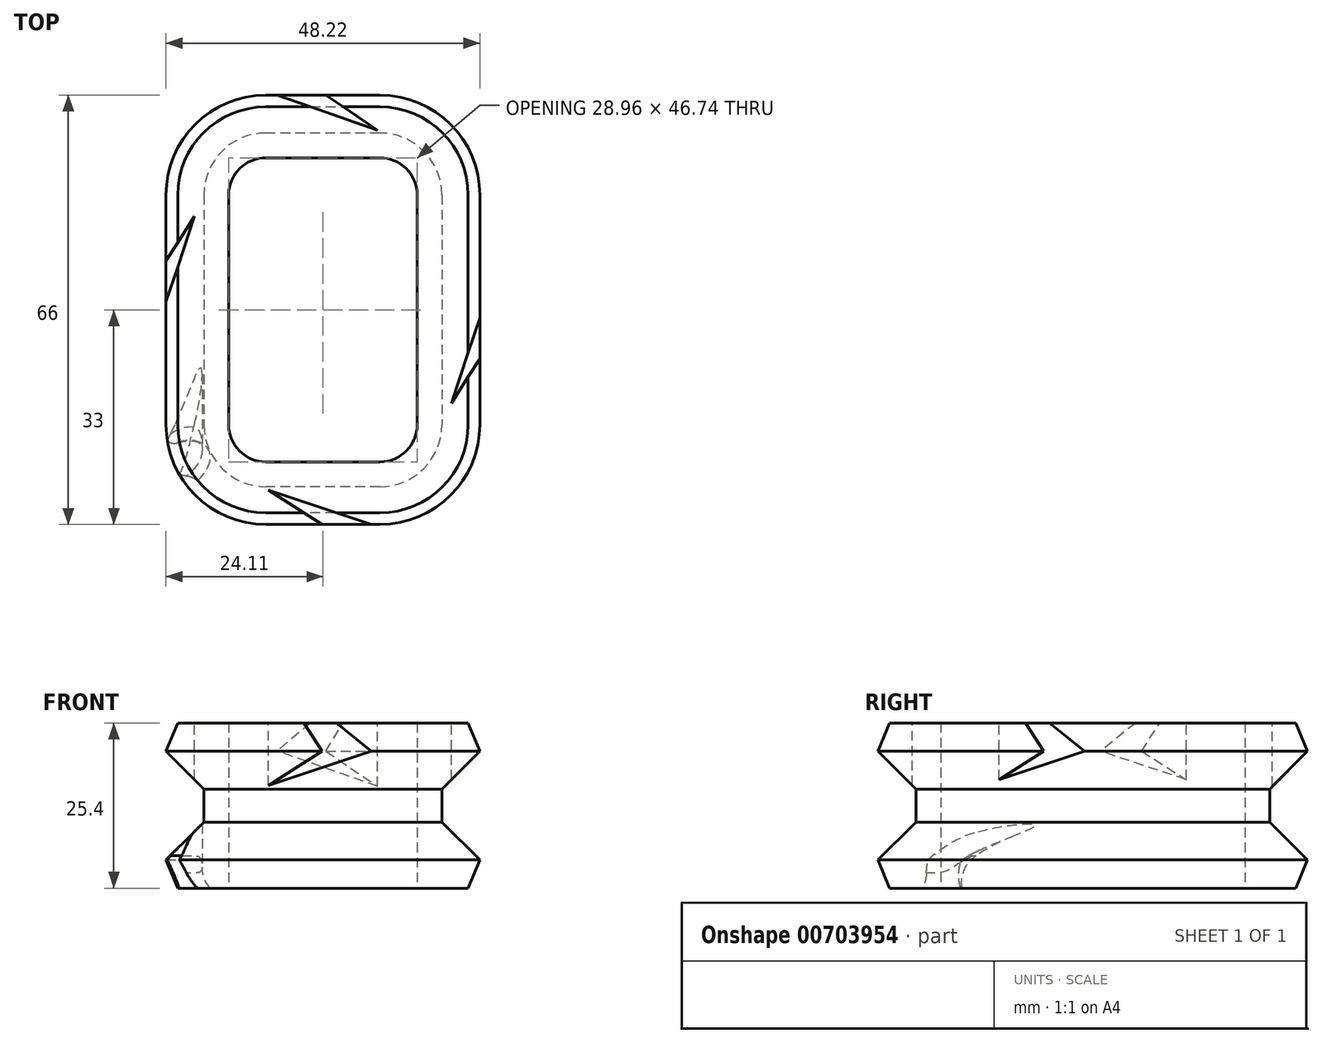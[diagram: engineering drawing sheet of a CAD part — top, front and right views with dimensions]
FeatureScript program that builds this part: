
annotation { "Feature Type Name" : "Feature", "Feature Type Description" : "" }
export const myFeature = defineFeature(function(context is Context, id is Id, definition is map)
    precondition{}
    {
        {
            var Q0;
            Q0=qCreatedBy(makeId("Top.planeOp"),FACE);
            var sketch = newSketch(context, id + "F0", { "sketchPlane" : qUnion([Q0])});
            skLineSegment(sketch, "E0.bottom", {"start": v(8.76, 23.37) * mm, "end": v(-8.76, 23.37) * mm});
            skLineSegment(sketch, "E0.top", {"start": v(8.76, -23.37) * mm, "end": v(-8.76, -23.37) * mm});
            skLineSegment(sketch, "E0.left", {"start": v(14.48, 17.65) * mm, "end": v(14.48, -17.65) * mm});
            skLineSegment(sketch, "E0.right", {"start": v(-14.48, 17.65) * mm, "end": v(-14.48, -17.65) * mm});
            skPoint(sketch, "E0.middle", {"position": v(0, 0) * mm});
            skPoint(sketch, "E1.visualSharp", {"position": v(-14.48, 23.37) * mm});
            skArc(sketch, "E1.filletArc", {"start": v(-8.76, 23.37) * mm, "mid": v(-12.8, 21.7) * mm, "end": v(-14.48, 17.65) * mm});
            skPoint(sketch, "E2.visualSharp", {"position": v(14.48, 23.37) * mm});
            skArc(sketch, "E2.filletArc", {"start": v(14.48, 17.65) * mm, "mid": v(12.8, 21.7) * mm, "end": v(8.76, 23.37) * mm});
            skPoint(sketch, "E3.visualSharp", {"position": v(14.48, -23.37) * mm});
            skArc(sketch, "E3.filletArc", {"start": v(8.76, -23.37) * mm, "mid": v(12.8, -21.7) * mm, "end": v(14.48, -17.65) * mm});
            skPoint(sketch, "E4.visualSharp", {"position": v(-14.48, -23.37) * mm});
            skArc(sketch, "E4.filletArc", {"start": v(-14.48, -17.65) * mm, "mid": v(-12.8, -21.7) * mm, "end": v(-8.76, -23.37) * mm});
            skLineSegment(sketch, "E5.0", {"start": v(-18.29, 17.65) * mm, "end": v(-18.29, -17.65) * mm});
            skArc(sketch, "E5.1", {"start": v(-8.76, 27.18) * mm, "mid": v(-15.5, 24.39) * mm, "end": v(-18.29, 17.65) * mm});
            skArc(sketch, "E5.2", {"start": v(-18.29, -17.65) * mm, "mid": v(-15.5, -24.39) * mm, "end": v(-8.76, -27.18) * mm});
            skLineSegment(sketch, "E5.3", {"start": v(8.76, 27.18) * mm, "end": v(-8.76, 27.18) * mm});
            skLineSegment(sketch, "E5.4", {"start": v(8.76, -27.18) * mm, "end": v(-8.76, -27.18) * mm});
            skArc(sketch, "E5.5", {"start": v(8.76, -27.18) * mm, "mid": v(15.5, -24.39) * mm, "end": v(18.29, -17.65) * mm});
            skLineSegment(sketch, "E5.6", {"start": v(18.29, 17.65) * mm, "end": v(18.29, -17.65) * mm});
            skArc(sketch, "E5.7", {"start": v(18.29, 17.65) * mm, "mid": v(15.5, 24.39) * mm, "end": v(8.76, 27.18) * mm});
            skArc(sketch, "E6.0", {"start": v(28.45, 17.65) * mm, "mid": v(22.68, 31.57) * mm, "end": v(8.76, 37.34) * mm});
            skLineSegment(sketch, "E6.1", {"start": v(28.45, 17.65) * mm, "end": v(28.45, -17.65) * mm});
            skLineSegment(sketch, "E6.2", {"start": v(8.76, 37.34) * mm, "end": v(-8.76, 37.34) * mm});
            skArc(sketch, "E6.3", {"start": v(8.76, -37.34) * mm, "mid": v(22.68, -31.57) * mm, "end": v(28.45, -17.65) * mm});
            skArc(sketch, "E6.4", {"start": v(-8.76, 37.34) * mm, "mid": v(-22.68, 31.57) * mm, "end": v(-28.45, 17.65) * mm});
            skLineSegment(sketch, "E6.5", {"start": v(-28.45, 17.65) * mm, "end": v(-28.45, -17.65) * mm});
            skArc(sketch, "E6.6", {"start": v(-28.45, -17.65) * mm, "mid": v(-22.68, -31.57) * mm, "end": v(-8.76, -37.34) * mm});
            skLineSegment(sketch, "E6.7", {"start": v(8.76, -37.34) * mm, "end": v(-8.76, -37.34) * mm});
            skSolve(sketch);
        }
        {
            var Q0;
            Q0=makeQuery(id+"F0.imprint","IMPRINT",FACE,{"disambiguationData":[TD([[makeQuery(id+"F0.imprint","IMPRINT",EDGE,{"derivedFrom":sQuery(id+"F0.wireOp",EDGE,"E0.bottom")}),-1.0]])]});
            extrude(context, id + "F1", {"entities" : qUnion([Q0]), "depth" : 25.4 * mm, "offsetDistance" : 25.4 * mm});
        }
        {
            var Q0;
            Q0=qCreatedBy(makeId("Top.planeOp"),FACE);
            cPlane(context, id + "F2", {"entities" : qUnion([Q0]), "cplaneType" : CPlaneType.OFFSET, "offset" : 25.4 * mm, "width" : 152.4 * mm, "height" : 152.4 * mm});
        }
        {
            var Q0;
            Q0=makeQuery(id+"F0.imprint","IMPRINT",FACE,{"disambiguationData":[TD([[makeQuery(id+"F0.imprint","IMPRINT",EDGE,{"derivedFrom":sQuery(id+"F0.wireOp",EDGE,"E5.0")}),-1.0]])]});
            extrude(context, id + "F3", {"entities" : qUnion([Q0]), "operationType" : NewBodyOperationType.ADD, "depth" : 10.16 * mm, "offsetDistance" : 25.4 * mm});
        }
        {
            var Q0;
            Q0=makeQuery(id+"F3.opExtrude","CAP_EDGE",EDGE,{"disambiguationData":[OSD([sQuery(id+"F0.wireOp",EDGE,"E6.7")])],"isStart":false});
            chamfer(context, id + "F4", {"entities" : qUnion([Q0]), "width" : 10.16 * mm, "tangentPropagation" : true});
        }
        {
            var Q0;
            {var subQ0=sQuery(id+"F0.wireOp",EDGE,"E6.3");var subQ1=sQuery(id+"F0.wireOp",EDGE,"E5.7");var subQ2=sQuery(id+"F0.wireOp",EDGE,"E5.6");var subQ3=sQuery(id+"F0.wireOp",EDGE,"E5.5");var subQ4=sQuery(id+"F0.wireOp",EDGE,"E5.4");var subQ5=sQuery(id+"F0.wireOp",EDGE,"E5.3");var subQ6=sQuery(id+"F0.wireOp",EDGE,"E5.2");var subQ7=sQuery(id+"F0.wireOp",EDGE,"E5.1");var subQ8=sQuery(id+"F0.wireOp",EDGE,"E5.0");Q0=makeQuery(id+"F4.opChamfer","BLEND_EDGE",EDGE,{"blendedFrom":[makeQuery(id+"F3.opExtrude","CAP_EDGE",EDGE,{"disambiguationData":[OSD([subQ0])],"isStart":false}),makeQuery(id+"F3.boolean.opBoolean","MERGE",FACE,{"derivedFrom":[makeQuery(id+"F1.opExtrude","CAP_FACE",FACE,{"disambiguationData":[OSD([sQuery(id+"F0.wireOp",EDGE,"E0.bottom"),sQuery(id+"F0.wireOp",EDGE,"E0.top"),sQuery(id+"F0.wireOp",EDGE,"E0.left"),sQuery(id+"F0.wireOp",EDGE,"E0.right"),sQuery(id+"F0.wireOp",EDGE,"E1.filletArc"),sQuery(id+"F0.wireOp",EDGE,"E2.filletArc"),sQuery(id+"F0.wireOp",EDGE,"E3.filletArc"),sQuery(id+"F0.wireOp",EDGE,"E4.filletArc"),subQ8,subQ7,subQ6,subQ5,subQ4,subQ3,subQ2,subQ1])],"isStart":true}),makeQuery(id+"F3.opExtrude","CAP_FACE",FACE,{"disambiguationData":[OSD([subQ8,subQ7,subQ6,subQ5,subQ4,subQ3,subQ2,subQ1,sQuery(id+"F0.wireOp",EDGE,"E6.0"),sQuery(id+"F0.wireOp",EDGE,"E6.1"),sQuery(id+"F0.wireOp",EDGE,"E6.2"),subQ0,sQuery(id+"F0.wireOp",EDGE,"E6.4"),sQuery(id+"F0.wireOp",EDGE,"E6.5"),sQuery(id+"F0.wireOp",EDGE,"E6.6"),sQuery(id+"F0.wireOp",EDGE,"E6.7")])],"isStart":true})]})],"blendedInto":[makeQuery(id+"F3.boolean.opBoolean","MERGE",FACE,{"derivedFrom":[makeQuery(id+"F1.opExtrude","CAP_FACE",FACE,{"disambiguationData":[OSD([sQuery(id+"F0.wireOp",EDGE,"E0.bottom"),sQuery(id+"F0.wireOp",EDGE,"E0.top"),sQuery(id+"F0.wireOp",EDGE,"E0.left"),sQuery(id+"F0.wireOp",EDGE,"E0.right"),sQuery(id+"F0.wireOp",EDGE,"E1.filletArc"),sQuery(id+"F0.wireOp",EDGE,"E2.filletArc"),sQuery(id+"F0.wireOp",EDGE,"E3.filletArc"),sQuery(id+"F0.wireOp",EDGE,"E4.filletArc"),subQ8,subQ7,subQ6,subQ5,subQ4,subQ3,subQ2,subQ1])],"isStart":true}),makeQuery(id+"F3.opExtrude","CAP_FACE",FACE,{"disambiguationData":[OSD([subQ8,subQ7,subQ6,subQ5,subQ4,subQ3,subQ2,subQ1,sQuery(id+"F0.wireOp",EDGE,"E6.0"),sQuery(id+"F0.wireOp",EDGE,"E6.1"),sQuery(id+"F0.wireOp",EDGE,"E6.2"),subQ0,sQuery(id+"F0.wireOp",EDGE,"E6.4"),sQuery(id+"F0.wireOp",EDGE,"E6.5"),sQuery(id+"F0.wireOp",EDGE,"E6.6"),sQuery(id+"F0.wireOp",EDGE,"E6.7")])],"isStart":true})]})]});}
            chamfer(context, id + "F5", {"entities" : qUnion([Q0]), "width" : 2.54 * mm, "tangentPropagation" : true});
        }
        {
            var Q0;
            Q0=qCreatedBy(id+"F2.planeOp",FACE);
            var sketch = newSketch(context, id + "F6", { "sketchPlane" : qUnion([Q0])});
            skArc(sketch, "E7.0", {"start": v(28.45, 17.65) * mm, "mid": v(22.68, 31.57) * mm, "end": v(8.76, 37.34) * mm});
            skLineSegment(sketch, "E7.1", {"start": v(28.45, 17.65) * mm, "end": v(28.45, -17.65) * mm});
            skLineSegment(sketch, "E7.2", {"start": v(8.76, 37.34) * mm, "end": v(-8.76, 37.34) * mm});
            skArc(sketch, "E7.3", {"start": v(8.76, -37.34) * mm, "mid": v(22.68, -31.57) * mm, "end": v(28.45, -17.65) * mm});
            skArc(sketch, "E7.4", {"start": v(-8.76, 37.34) * mm, "mid": v(-22.68, 31.57) * mm, "end": v(-28.45, 17.65) * mm});
            skLineSegment(sketch, "E7.5", {"start": v(-28.45, 17.65) * mm, "end": v(-28.45, -17.65) * mm});
            skArc(sketch, "E7.6", {"start": v(-28.45, -17.65) * mm, "mid": v(-22.68, -31.57) * mm, "end": v(-8.76, -37.34) * mm});
            skLineSegment(sketch, "E7.7", {"start": v(8.76, -37.34) * mm, "end": v(-8.76, -37.34) * mm});
            skLineSegment(sketch, "E8.0", {"start": v(8.76, 27.18) * mm, "end": v(-8.76, 27.18) * mm});
            skArc(sketch, "E8.1", {"start": v(18.29, 17.65) * mm, "mid": v(15.5, 24.39) * mm, "end": v(8.76, 27.18) * mm});
            skArc(sketch, "E8.2", {"start": v(-8.76, 27.18) * mm, "mid": v(-15.5, 24.39) * mm, "end": v(-18.29, 17.65) * mm});
            skLineSegment(sketch, "E8.3", {"start": v(18.29, 17.65) * mm, "end": v(18.29, -17.65) * mm});
            skLineSegment(sketch, "E8.4", {"start": v(-18.29, 17.65) * mm, "end": v(-18.29, -17.65) * mm});
            skArc(sketch, "E8.5", {"start": v(-18.29, -17.65) * mm, "mid": v(-15.5, -24.39) * mm, "end": v(-8.76, -27.18) * mm});
            skLineSegment(sketch, "E8.6", {"start": v(8.76, -27.18) * mm, "end": v(-8.76, -27.18) * mm});
            skArc(sketch, "E8.7", {"start": v(8.76, -27.18) * mm, "mid": v(15.5, -24.39) * mm, "end": v(18.29, -17.65) * mm});
            skSolve(sketch);
        }
        {
            var Q0;
            Q0=makeQuery(id+"F6.imprint","IMPRINT",FACE,{"disambiguationData":[TD([[makeQuery(id+"F6.imprint","IMPRINT",EDGE,{"derivedFrom":sQuery(id+"F6.wireOp",EDGE,"E7.0")}),1.0]])]});
            extrude(context, id + "F7", {"entities" : qUnion([Q0]), "operationType" : NewBodyOperationType.ADD, "oppositeDirection" : true, "depth" : 10.16 * mm, "offsetDistance" : 25.4 * mm});
        }
        {
            var Q0;
            Q0=makeQuery(id+"F7.opExtrude","CAP_EDGE",EDGE,{"disambiguationData":[OSD([sQuery(id+"F6.wireOp",EDGE,"E7.7")])],"isStart":false});
            chamfer(context, id + "F8", {"entities" : qUnion([Q0]), "width" : 10.16 * mm, "tangentPropagation" : true});
        }
        {
            var Q0;
            {var subQ0=sQuery(id+"F6.wireOp",EDGE,"E7.7");Q0=makeQuery(id+"F8.opChamfer","BLEND_EDGE",EDGE,{"blendedFrom":[makeQuery(id+"F7.opExtrude","CAP_EDGE",EDGE,{"disambiguationData":[OSD([subQ0])],"isStart":false}),makeQuery(id+"F7.boolean.opBoolean","MERGE",FACE,{"derivedFrom":[makeQuery(id+"F1.opExtrude","CAP_FACE",FACE,{"disambiguationData":[OSD([sQuery(id+"F0.wireOp",EDGE,"E0.bottom"),sQuery(id+"F0.wireOp",EDGE,"E0.top"),sQuery(id+"F0.wireOp",EDGE,"E0.left"),sQuery(id+"F0.wireOp",EDGE,"E0.right"),sQuery(id+"F0.wireOp",EDGE,"E1.filletArc"),sQuery(id+"F0.wireOp",EDGE,"E2.filletArc"),sQuery(id+"F0.wireOp",EDGE,"E3.filletArc"),sQuery(id+"F0.wireOp",EDGE,"E4.filletArc"),sQuery(id+"F0.wireOp",EDGE,"E5.0"),sQuery(id+"F0.wireOp",EDGE,"E5.1"),sQuery(id+"F0.wireOp",EDGE,"E5.2"),sQuery(id+"F0.wireOp",EDGE,"E5.3"),sQuery(id+"F0.wireOp",EDGE,"E5.4"),sQuery(id+"F0.wireOp",EDGE,"E5.5"),sQuery(id+"F0.wireOp",EDGE,"E5.6"),sQuery(id+"F0.wireOp",EDGE,"E5.7")])],"isStart":false}),makeQuery(id+"F7.opExtrude","CAP_FACE",FACE,{"disambiguationData":[OSD([sQuery(id+"F6.wireOp",EDGE,"E7.0"),sQuery(id+"F6.wireOp",EDGE,"E7.1"),sQuery(id+"F6.wireOp",EDGE,"E7.2"),sQuery(id+"F6.wireOp",EDGE,"E7.3"),sQuery(id+"F6.wireOp",EDGE,"E7.4"),sQuery(id+"F6.wireOp",EDGE,"E7.5"),sQuery(id+"F6.wireOp",EDGE,"E7.6"),subQ0,sQuery(id+"F6.wireOp",EDGE,"E8.0"),sQuery(id+"F6.wireOp",EDGE,"E8.1"),sQuery(id+"F6.wireOp",EDGE,"E8.2"),sQuery(id+"F6.wireOp",EDGE,"E8.3"),sQuery(id+"F6.wireOp",EDGE,"E8.4"),sQuery(id+"F6.wireOp",EDGE,"E8.5"),sQuery(id+"F6.wireOp",EDGE,"E8.6"),sQuery(id+"F6.wireOp",EDGE,"E8.7")])],"isStart":true})]})],"blendedInto":[makeQuery(id+"F7.boolean.opBoolean","MERGE",FACE,{"derivedFrom":[makeQuery(id+"F1.opExtrude","CAP_FACE",FACE,{"disambiguationData":[OSD([sQuery(id+"F0.wireOp",EDGE,"E0.bottom"),sQuery(id+"F0.wireOp",EDGE,"E0.top"),sQuery(id+"F0.wireOp",EDGE,"E0.left"),sQuery(id+"F0.wireOp",EDGE,"E0.right"),sQuery(id+"F0.wireOp",EDGE,"E1.filletArc"),sQuery(id+"F0.wireOp",EDGE,"E2.filletArc"),sQuery(id+"F0.wireOp",EDGE,"E3.filletArc"),sQuery(id+"F0.wireOp",EDGE,"E4.filletArc"),sQuery(id+"F0.wireOp",EDGE,"E5.0"),sQuery(id+"F0.wireOp",EDGE,"E5.1"),sQuery(id+"F0.wireOp",EDGE,"E5.2"),sQuery(id+"F0.wireOp",EDGE,"E5.3"),sQuery(id+"F0.wireOp",EDGE,"E5.4"),sQuery(id+"F0.wireOp",EDGE,"E5.5"),sQuery(id+"F0.wireOp",EDGE,"E5.6"),sQuery(id+"F0.wireOp",EDGE,"E5.7")])],"isStart":false}),makeQuery(id+"F7.opExtrude","CAP_FACE",FACE,{"disambiguationData":[OSD([sQuery(id+"F6.wireOp",EDGE,"E7.0"),sQuery(id+"F6.wireOp",EDGE,"E7.1"),sQuery(id+"F6.wireOp",EDGE,"E7.2"),sQuery(id+"F6.wireOp",EDGE,"E7.3"),sQuery(id+"F6.wireOp",EDGE,"E7.4"),sQuery(id+"F6.wireOp",EDGE,"E7.5"),sQuery(id+"F6.wireOp",EDGE,"E7.6"),subQ0,sQuery(id+"F6.wireOp",EDGE,"E8.0"),sQuery(id+"F6.wireOp",EDGE,"E8.1"),sQuery(id+"F6.wireOp",EDGE,"E8.2"),sQuery(id+"F6.wireOp",EDGE,"E8.3"),sQuery(id+"F6.wireOp",EDGE,"E8.4"),sQuery(id+"F6.wireOp",EDGE,"E8.5"),sQuery(id+"F6.wireOp",EDGE,"E8.6"),sQuery(id+"F6.wireOp",EDGE,"E8.7")])],"isStart":true})]})]});}
            chamfer(context, id + "F9", {"entities" : qUnion([Q0]), "width" : 2.54 * mm, "tangentPropagation" : true});
        }
        {
            var Q0;
            Q0=qCreatedBy(makeId("Right.planeOp"),FACE);
            cPlane(context, id + "F10", {"entities" : qUnion([Q0]), "cplaneType" : CPlaneType.OFFSET, "offset" : 20.32 * mm, "oppositeDirection" : true, "width" : 152.4 * mm, "height" : 152.4 * mm});
        }
        {
            var Q0;
            Q0=qCreatedBy(id+"F10.planeOp",FACE);
            var sketch = newSketch(context, id + "F11", { "sketchPlane" : qUnion([Q0])});
            skFitSpline(sketch, "E9", {"points": [v(-24.66, -12.7) * mm, v(-21.88, 3.4) * mm, v(0, 12.85) * mm, v(9.24, 13.4) * mm], "startDerivative": vector(2.56, 51.63) * mm, "endDerivative": vector(30.58, -0.85) * mm});
            skSolve(sketch);
        }
        {
            var Q0;
            Q0=qCreatedBy(makeId("Top.planeOp"),FACE);
            cPlane(context, id + "F12", {"entities" : qUnion([Q0]), "cplaneType" : CPlaneType.OFFSET, "offset" : 7.62 * mm, "oppositeDirection" : true, "width" : 152.4 * mm, "height" : 152.4 * mm});
        }
        {
            var Q0;
            Q0=qCreatedBy(id+"F12.planeOp",FACE);
            var sketch = newSketch(context, id + "F13", { "sketchPlane" : qUnion([Q0])});
            skFitSpline(sketch, "E10", {"points": [v(-29.95, -29.23) * mm, v(-23.21, -23.7) * mm, v(-18.64, -23.8) * mm, v(-22.25, -28.06) * mm, v(-30.23, -30.68) * mm, v(-29.95, -29.23) * mm]});
            skSolve(sketch);
        }
        {
            var Q0;
            Q0=makeQuery(id+"F13.imprint","IMPRINT",FACE,{"disambiguationData":[TD([[makeQuery(id+"F13.imprint","IMPRINT",EDGE,{"derivedFrom":sQuery(id+"F13.wireOp",EDGE,"E10")}),-1.0]])]});
            var Q1;
            Q1=sQuery(id+"F11.wireOp",EDGE,"E9");
            sweep(context, id + "F14", {"operationType" : NewBodyOperationType.REMOVE, "profiles" : qUnion([Q0]), "path" : qUnion([Q1])});
        }
        {
            var Q0;
            {var subQ0=sQuery(id+"F0.wireOp",EDGE,"E5.7");var subQ1=sQuery(id+"F0.wireOp",EDGE,"E5.6");var subQ2=sQuery(id+"F0.wireOp",EDGE,"E5.5");var subQ3=sQuery(id+"F0.wireOp",EDGE,"E5.4");var subQ4=sQuery(id+"F0.wireOp",EDGE,"E5.3");var subQ5=sQuery(id+"F0.wireOp",EDGE,"E5.2");var subQ6=sQuery(id+"F0.wireOp",EDGE,"E5.1");var subQ7=sQuery(id+"F0.wireOp",EDGE,"E5.0");Q0=makeQuery(id+"F14.boolean.opBoolean","INTERSECT",EDGE,{"derivedFrom":[makeQuery(id+"F3.boolean.opBoolean","MERGE",FACE,{"derivedFrom":[makeQuery(id+"F1.opExtrude","CAP_FACE",FACE,{"disambiguationData":[OSD([sQuery(id+"F0.wireOp",EDGE,"E0.bottom"),sQuery(id+"F0.wireOp",EDGE,"E0.top"),sQuery(id+"F0.wireOp",EDGE,"E0.left"),sQuery(id+"F0.wireOp",EDGE,"E0.right"),sQuery(id+"F0.wireOp",EDGE,"E1.filletArc"),sQuery(id+"F0.wireOp",EDGE,"E2.filletArc"),sQuery(id+"F0.wireOp",EDGE,"E3.filletArc"),sQuery(id+"F0.wireOp",EDGE,"E4.filletArc"),subQ7,subQ6,subQ5,subQ4,subQ3,subQ2,subQ1,subQ0])],"isStart":true}),makeQuery(id+"F3.opExtrude","CAP_FACE",FACE,{"disambiguationData":[OSD([subQ7,subQ6,subQ5,subQ4,subQ3,subQ2,subQ1,subQ0,sQuery(id+"F0.wireOp",EDGE,"E6.0"),sQuery(id+"F0.wireOp",EDGE,"E6.1"),sQuery(id+"F0.wireOp",EDGE,"E6.2"),sQuery(id+"F0.wireOp",EDGE,"E6.3"),sQuery(id+"F0.wireOp",EDGE,"E6.4"),sQuery(id+"F0.wireOp",EDGE,"E6.5"),sQuery(id+"F0.wireOp",EDGE,"E6.6"),sQuery(id+"F0.wireOp",EDGE,"E6.7")])],"isStart":true})]}),makeQuery(id+"F14.opSweep","SWEPT_FACE",FACE,{"disambiguationData":[OSD([sQuery(id+"F11.wireOp",EDGE,"E9"),sQuery(id+"F13.wireOp",EDGE,"E10")])]})]});}
            chamfer(context, id + "F15", {"entities" : qUnion([Q0]), "width" : 1.27 * mm, "tangentPropagation" : true});
        }
        {
            var Q0;
            {var subQ0=makeQuery(id+"F14.opSweep","SWEPT_FACE",FACE,{"disambiguationData":[OSD([sQuery(id+"F11.wireOp",EDGE,"E9"),sQuery(id+"F13.wireOp",EDGE,"E10")])]});var subQ1=sQuery(id+"F0.wireOp",EDGE,"E5.7");var subQ2=sQuery(id+"F0.wireOp",EDGE,"E5.6");var subQ3=sQuery(id+"F0.wireOp",EDGE,"E5.5");var subQ4=sQuery(id+"F0.wireOp",EDGE,"E5.4");var subQ5=sQuery(id+"F0.wireOp",EDGE,"E5.3");var subQ6=sQuery(id+"F0.wireOp",EDGE,"E5.2");var subQ7=sQuery(id+"F0.wireOp",EDGE,"E5.1");var subQ8=sQuery(id+"F0.wireOp",EDGE,"E5.0");Q0=makeQuery(id+"F15.opChamfer","BLEND_EDGE",EDGE,{"blendedFrom":[makeQuery(id+"F14.boolean.opBoolean","INTERSECT",EDGE,{"derivedFrom":[makeQuery(id+"F3.boolean.opBoolean","MERGE",FACE,{"derivedFrom":[makeQuery(id+"F1.opExtrude","CAP_FACE",FACE,{"disambiguationData":[OSD([sQuery(id+"F0.wireOp",EDGE,"E0.bottom"),sQuery(id+"F0.wireOp",EDGE,"E0.top"),sQuery(id+"F0.wireOp",EDGE,"E0.left"),sQuery(id+"F0.wireOp",EDGE,"E0.right"),sQuery(id+"F0.wireOp",EDGE,"E1.filletArc"),sQuery(id+"F0.wireOp",EDGE,"E2.filletArc"),sQuery(id+"F0.wireOp",EDGE,"E3.filletArc"),sQuery(id+"F0.wireOp",EDGE,"E4.filletArc"),subQ8,subQ7,subQ6,subQ5,subQ4,subQ3,subQ2,subQ1])],"isStart":true}),makeQuery(id+"F3.opExtrude","CAP_FACE",FACE,{"disambiguationData":[OSD([subQ8,subQ7,subQ6,subQ5,subQ4,subQ3,subQ2,subQ1,sQuery(id+"F0.wireOp",EDGE,"E6.0"),sQuery(id+"F0.wireOp",EDGE,"E6.1"),sQuery(id+"F0.wireOp",EDGE,"E6.2"),sQuery(id+"F0.wireOp",EDGE,"E6.3"),sQuery(id+"F0.wireOp",EDGE,"E6.4"),sQuery(id+"F0.wireOp",EDGE,"E6.5"),sQuery(id+"F0.wireOp",EDGE,"E6.6"),sQuery(id+"F0.wireOp",EDGE,"E6.7")])],"isStart":true})]}),subQ0]}),makeQuery(id+"F14.boolean.opBoolean","COPY",FACE,{"derivedFrom":subQ0})],"blendedInto":[makeQuery(id+"F14.boolean.opBoolean","COPY",FACE,{"derivedFrom":subQ0})]});}
            fillet(context, id + "F16", {"entities" : qUnion([Q0]), "radius" : 5.08 * mm, "tangentPropagation" : true, "allowEdgeOverflow" : false});
        }
        {
            var Q0;
            Q0=qCreatedBy(makeId("Top.planeOp"),FACE);
            cPlane(context, id + "F17", {"entities" : qUnion([Q0]), "cplaneType" : CPlaneType.OFFSET, "offset" : 25.4 * mm, "width" : 152.4 * mm, "height" : 152.4 * mm});
        }
        {
            var Q0;
            Q0=qCreatedBy(id+"F17.planeOp",FACE);
            var sketch = newSketch(context, id + "F18", { "sketchPlane" : qUnion([Q0])});
            skLineSegment(sketch, "E11", {"start": v(-27.72, -9.61) * mm, "end": v(-19.73, 14.37) * mm});
            skLineSegment(sketch, "E12", {"start": v(-19.73, 14.37) * mm, "end": v(-31.13, -3.5) * mm});
            skLineSegment(sketch, "E13", {"start": v(-31.13, -3.5) * mm, "end": v(-27.72, -9.61) * mm});
            skLineSegment(sketch, "E14.1.0", {"start": v(-8.38, -27.72) * mm, "end": v(9.48, -39.12) * mm});
            skLineSegment(sketch, "E14.1.1", {"start": v(15.6, -35.72) * mm, "end": v(-8.38, -27.72) * mm});
            skLineSegment(sketch, "E14.1.2", {"start": v(9.48, -39.12) * mm, "end": v(15.6, -35.72) * mm});
            skLineSegment(sketch, "E14.2.0", {"start": v(19.73, -14.37) * mm, "end": v(31.13, 3.5) * mm});
            skLineSegment(sketch, "E14.2.1", {"start": v(27.72, 9.61) * mm, "end": v(19.73, -14.37) * mm});
            skLineSegment(sketch, "E14.2.2", {"start": v(31.13, 3.5) * mm, "end": v(27.72, 9.61) * mm});
            skLineSegment(sketch, "E14.3.0", {"start": v(8.38, 27.6) * mm, "end": v(-8.38, 39) * mm});
            skLineSegment(sketch, "E14.3.1", {"start": v(-14.5, 35.6) * mm, "end": v(8.38, 27.6) * mm});
            skLineSegment(sketch, "E14.3.2", {"start": v(-8.38, 39) * mm, "end": v(-14.5, 35.6) * mm});
            skPoint(sketch, "E14.center", {"position": v(0, 0) * mm});
            skSolve(sketch);
        }
        {
            var Q0;
            Q0=makeQuery(id+"F18.imprint","IMPRINT",FACE,{"disambiguationData":[TD([[makeQuery(id+"F18.imprint","IMPRINT",EDGE,{"derivedFrom":sQuery(id+"F18.wireOp",EDGE,"E11")}),1.0]])]});
            var Q1;
            Q1=makeQuery(id+"F18.imprint","IMPRINT",FACE,{"disambiguationData":[TD([[makeQuery(id+"F18.imprint","IMPRINT",EDGE,{"derivedFrom":sQuery(id+"F18.wireOp",EDGE,"E14.3.0")}),1.0]])]});
            var Q2;
            Q2=makeQuery(id+"F18.imprint","IMPRINT",FACE,{"disambiguationData":[TD([[makeQuery(id+"F18.imprint","IMPRINT",EDGE,{"derivedFrom":sQuery(id+"F18.wireOp",EDGE,"E14.2.0")}),1.0]])]});
            var Q3;
            Q3=makeQuery(id+"F18.imprint","IMPRINT",FACE,{"disambiguationData":[TD([[makeQuery(id+"F18.imprint","IMPRINT",EDGE,{"derivedFrom":sQuery(id+"F18.wireOp",EDGE,"E14.1.0")}),1.0]])]});
            extrude(context, id + "F19", {"entities" : qUnion([Q0, Q1, Q2, Q3]), "operationType" : NewBodyOperationType.REMOVE, "oppositeDirection" : true, "depth" : 12.7 * mm, "offsetDistance" : 25.4 * mm});
        }
    });
